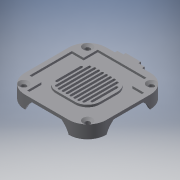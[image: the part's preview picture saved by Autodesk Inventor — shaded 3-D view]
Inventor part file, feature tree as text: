
AUTODESK INVENTOR PART (.ipt)
format: ipt  version: 2018 (Build 220112000, 112)  size: 600,064 bytes
history: native  units: mm
features: reference x24, extrude x7, sketch x6, projected_geometry x5, chamfer x4, fillet x3, other x3, plane x1
ambient origin geometry x8: Origin, YZ Plane, XZ Plane, XY Plane, X Axis, Y Axis, Z Axis, Center Point
bodies: Volumenkörper1 (feature_tree)
feature tree (53):
  extrude  "Extrusion1"  Depth=2.5mm TaperAngle=0.0deg
  extrude  "Extrusion2"  Depth=3.0mm
  sketch  "Skizze3"  dims[d9=30.0mm d10=6.0mm]
  sketch  "Skizze4"  dims[d11=6.0mm d13=6.0mm]
  plane  "Arbeitsebene1"
  extrude  "Extrusion3"  Depth=6.0mm
  extrude  "Extrusion4"  Depth=6.0mm
  chamfer  "Fase1"  Distance=6.5mm
  extrude  "Extrusion5"  Depth=1.25mm TaperAngle=45.0deg
  fillet  "Rundung1"  Radius=9.0mm
  chamfer  "Fase3"  Distance=9.0mm
  fillet  "Rundung2"  Radius=9.0mm
  chamfer  "Fase4"  Distance=9.0mm
  extrude  "Extrusion6"  Depth=1.25mm
  fillet  "Rundung3"  Radius=3.0mm
  chamfer  "Fase5"  Distance=13.0mm
  extrude  "Extrusion7"  Depth=1.25mm
  sketch  "Skizze1"  dims[d0=2.0mm d1=0.0mm d4=2.5mm d5=0.0mm]
  reference  "Referenz1"
  reference  "Referenz2"
  reference  "Referenz3"
  reference  "Referenz4"
  reference  "Referenz5"
  reference  "Referenz6"
  reference  "Referenz7"
  reference  "Referenz8"
  reference  "Referenz9"
  reference  "Referenz10"
  sketch  "Skizze2"  dims[d7=3.0mm d8=3.0mm]
  reference  "Referenz12"
  reference  "Referenz13"
  reference  "Referenz14"
  reference  "Referenz15"
  projected_geometry  "Projizierte Kontur1"
  projected_geometry  "Projizierte Kontur2"
  sketch  "Skizze5"  dims[d14=6.0mm d15=6.5mm d16=0.0mm]
  sketch  "Skizze6"  dims[d17=33.0mm d18=0.0mm d19=1.4mm d20=2.0mm d21=45.0deg d22=9.0mm d23=9.0mm d24=9.0mm d25=9.0mm d26=3.0mm d27=3.0mm d28=13.0mm d29=13.0mm d30=27.0mm d31=4.0mm d32=3.0mm d33=31.0mm d34=10.5mm d35=10.5mm d36=10.5mm d37=31.0mm d38=10.5mm d39=1.4mm d40=0.0mm d41=8.0mm d45=4.5mm d46=2.0mm d47=45.0deg d48=11.75mm d49=1.5mm d50=1.5mm d51=1.5mm d52=0.5mm d54=1.0mm d55=1.5mm d56=1.5mm d57=1.5mm d58=1.5mm d59=1.5mm d60=1.5mm d61=1.5mm d62=1.5mm d63=1.0mm d64=1.0mm d65=1.0mm d66=1.0mm d67=1.0mm d68=1.0mm d69=1.0mm d70=1.0mm d72=7.1mm d73=0.0mm d74=8.0mm d75=1.75mm d76=45.0deg d77=0.5mm d78=0.2mm d79=1.75mm d80=45.0deg d82=0.25mm d86=0.2mm d87=0.2mm d88=0.2mm d89=0.2mm d90=0.2mm d91=4.051543mm d92=1.5mm d93=1.25mm d94=0.0mm]
  projected_geometry  "Projizierte Kontur3"
  reference  "Referenz17"
  reference  "Referenz18"
  reference  "Referenz19"
  reference  "Referenz23"
  reference  "Referenz24"
  reference  "Referenz25"
  reference  "Referenz26"
  reference  "Referenz27"
  reference  "Referenz28"
  reference  "Referenz29"
  projected_geometry  "Projizierte Kontur4"
  projected_geometry  "Projizierte Kontur5"
  parser-record x1  (decoder bookkeeping rows leaked as tree rows — omitted from the tree; the rows remain in map.json)
  other  "VolumeKnob.iam"
  other  "Oberbau:1"
note: 1 file-system path scrubbed to <path> (originals preserved in map.json)
